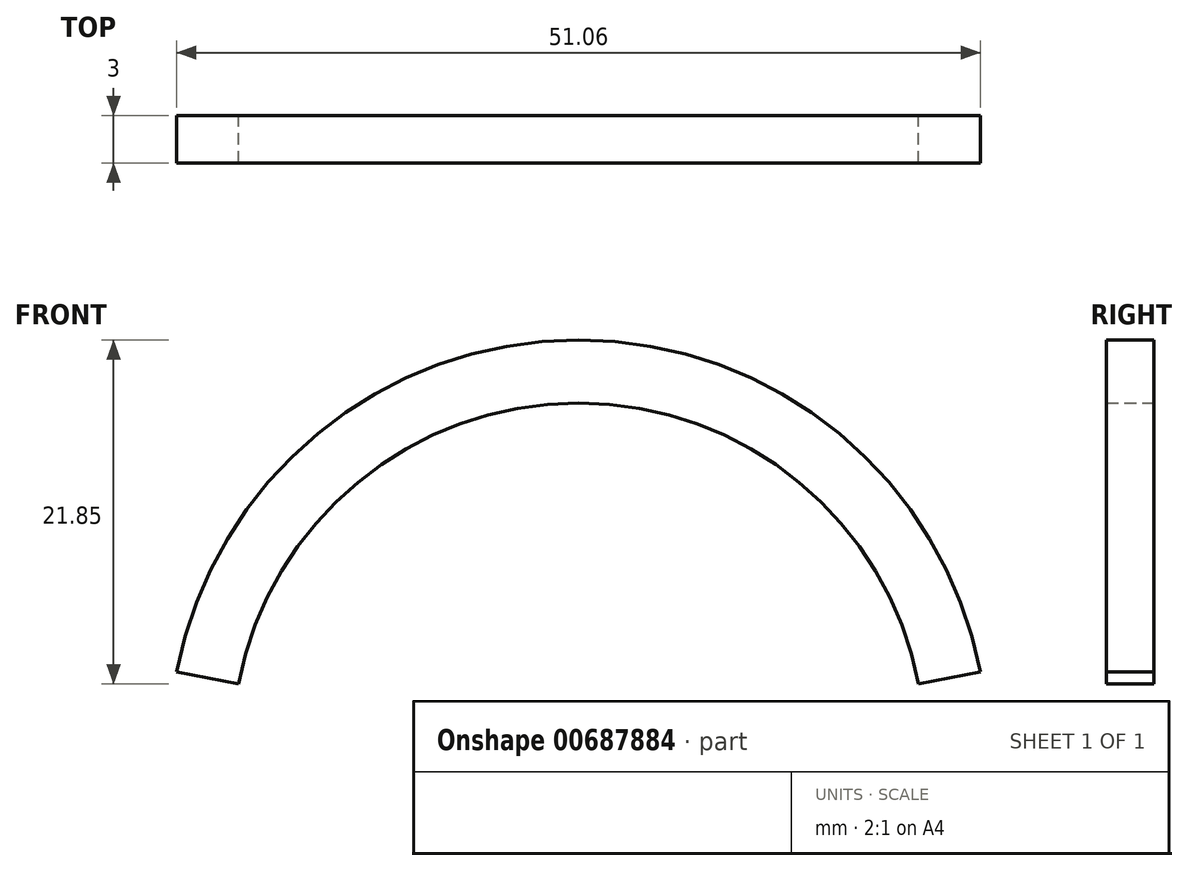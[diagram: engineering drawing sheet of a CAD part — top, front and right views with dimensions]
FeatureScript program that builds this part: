
annotation { "Feature Type Name" : "Feature", "Feature Type Description" : "" }
export const myFeature = defineFeature(function(context is Context, id is Id, definition is map)
    precondition{}
    {
        {
            var Q0;
            Q0=qCreatedBy(makeId("Front.planeOp"),FACE);
            var sketch = newSketch(context, id + "F0", { "sketchPlane" : qUnion([Q0])});
            skCircle(sketch, "E0", {"center": v(24.03, 28.35) * mm, "radius": 22 * mm});
            skCircle(sketch, "E1", {"center": v(24.03, 28.35) * mm, "radius": 26 * mm});
            skLineSegment(sketch, "E2", {"start": v(50.03, 28.35) * mm, "end": v(-1.97, 28.35) * mm});
            skLineSegment(sketch, "E3", {"start": v(-1.97, 28.35) * mm, "end": v(-1.97, 33.35) * mm});
            skLineSegment(sketch, "E4", {"start": v(-1.97, 33.35) * mm, "end": v(24.03, 28.35) * mm});
            skLineSegment(sketch, "E5", {"start": v(50.03, 28.35) * mm, "end": v(50.03, 33.35) * mm});
            skLineSegment(sketch, "E6", {"start": v(50.03, 33.35) * mm, "end": v(24.03, 28.35) * mm});
            skArc(sketch, "E7", {"start": v(161.05, 34.32) * mm, "mid": v(139.45, 52.17) * mm, "end": v(117.84, 34.32) * mm});
            skArc(sketch, "E8", {"start": v(164.98, 35.08) * mm, "mid": v(139.45, 56.17) * mm, "end": v(113.91, 35.08) * mm});
            skLineSegment(sketch, "E9", {"start": v(113.91, 35.08) * mm, "end": v(117.84, 34.32) * mm});
            skLineSegment(sketch, "E10", {"start": v(164.98, 35.08) * mm, "end": v(161.05, 34.32) * mm});
            skSolve(sketch);
        }
        {
            var Q0;
            {var subQ0=sQuery(id+"F0.wireOp",EDGE,"E6");var subQ1=sQuery(id+"F0.wireOp",EDGE,"E0");var subQ2=makeQuery(id+"F0.imprint","INTERSECT",VERTEX,{"derivedFrom":[subQ1,subQ0]});Q0=makeQuery(id+"F0.imprint","IMPRINT",FACE,{"disambiguationData":[TD([[makeQuery(id+"F0.imprint","IMPRINT",EDGE,{"disambiguationData":[TD([[subQ2,-1.0]])],"derivedFrom":subQ1}),-1.0]])]});}
            extrude(context, id + "F1", {"entities" : qUnion([Q0]), "depth" : 3 * mm, "offsetDistance" : 25 * mm});
        }
    });
